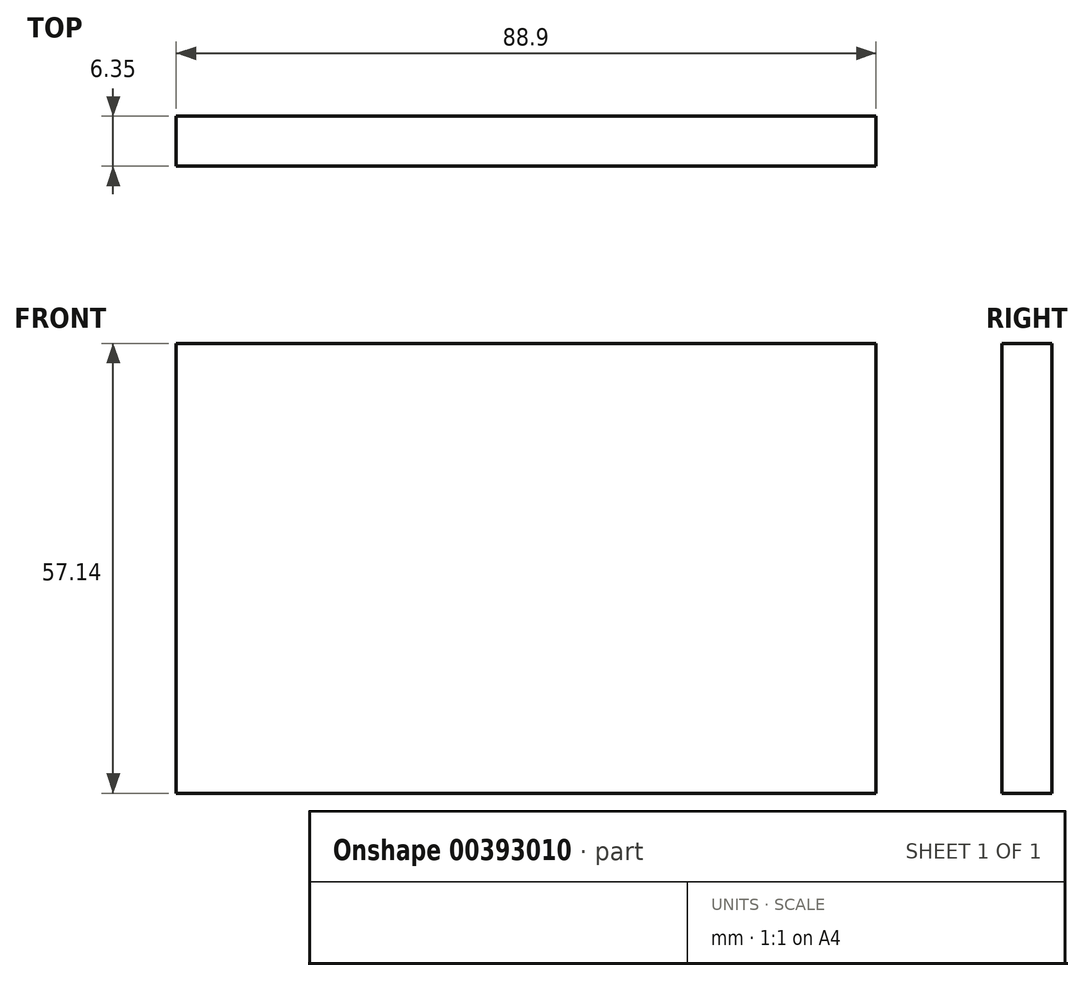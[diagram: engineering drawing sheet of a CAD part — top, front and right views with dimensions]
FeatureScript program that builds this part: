
annotation { "Feature Type Name" : "Feature", "Feature Type Description" : "" }
export const myFeature = defineFeature(function(context is Context, id is Id, definition is map)
    precondition{}
    {
        {
            var Q0;
            Q0=qCreatedBy(makeId("Front.planeOp"),FACE);
            var sketch = newSketch(context, id + "F0", { "sketchPlane" : qUnion([Q0])});
            skLineSegment(sketch, "E0.bottom", {"start": v(44.45, -28.58) * mm, "end": v(-44.45, -28.58) * mm});
            skLineSegment(sketch, "E0.top", {"start": v(44.45, 28.58) * mm, "end": v(-44.45, 28.58) * mm});
            skLineSegment(sketch, "E0.left", {"start": v(44.45, -28.58) * mm, "end": v(44.45, 28.58) * mm});
            skLineSegment(sketch, "E0.right", {"start": v(-44.45, -28.58) * mm, "end": v(-44.45, 28.57) * mm});
            skPoint(sketch, "E0.middle", {"position": v(0, 0) * mm});
            skSolve(sketch);
        }
        {
            var Q0;
            Q0=makeQuery(id+"F0.imprint","IMPRINT",FACE,{"disambiguationData":[TD([[makeQuery(id+"F0.imprint","IMPRINT",EDGE,{"derivedFrom":sQuery(id+"F0.wireOp",EDGE,"E0.bottom")}),-1.0]])]});
            extrude(context, id + "F1", {"entities" : qUnion([Q0]), "depth" : 6.35 * mm});
        }
    });
